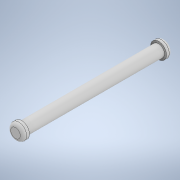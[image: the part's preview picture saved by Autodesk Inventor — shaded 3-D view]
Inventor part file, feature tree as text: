
AUTODESK INVENTOR PART (.ipt)
format: ipt  version: 2021 (Build 250183000, 183)  size: 118,272 bytes
history: native  units: in
note: dims shown in document units (in); Inventor stores cm internally (conversion verified against a paired STEP export)
features: extrude x3, sketch x3, plane x2, fillet x1
ambient origin geometry x8: Origin, YZ Plane, XZ Plane, XY Plane, X Axis, Y Axis, Z Axis, Center Point
bodies: Solid1 (feature_tree)
feature tree (9):
  extrude  "Extrusion1"  Depth=1.3543in TaperAngle=0.0deg
  plane  "Work Plane1"
  extrude  "Extrusion2"  Depth=0.1575in
  plane  "Work Plane2"
  extrude  "Extrusion3"  TaperAngle=0.0deg  [1 undecoded]
  fillet  "Fillet1"  Radius=0.0591in
  sketch  "Sketch1"  dims[d0=0.1181in d1=1.3543in d2=0.0in]
  sketch  "Sketch2"  dims[d3=0.0in d4=0.1575in]
  sketch  "Sketch3"  dims[d5=0.0591in d6=0.0in d7=0.0in d8=0.0591in d9=0.0in d10=0.0315in]
note: 1 required parameter value undecoded (feature->parameter linkage not recoverable at this tier; creation-order binding heuristic only, values carry confidence <= 0.55)
